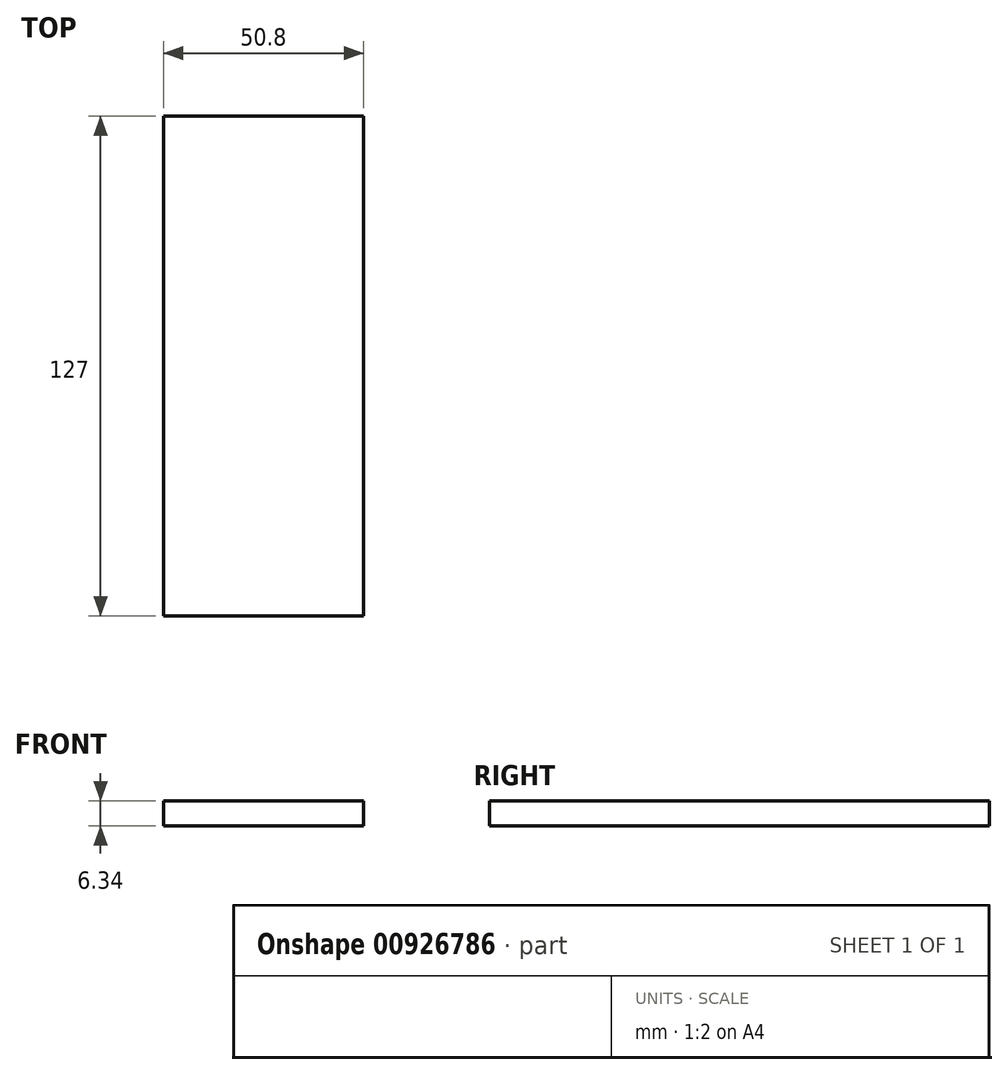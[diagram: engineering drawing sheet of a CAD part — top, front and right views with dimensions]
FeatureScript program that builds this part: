
annotation { "Feature Type Name" : "Feature", "Feature Type Description" : "" }
export const myFeature = defineFeature(function(context is Context, id is Id, definition is map)
    precondition{}
    {
        {
            var Q0;
            Q0=qCreatedBy(makeId("Front.planeOp"),FACE);
            var sketch = newSketch(context, id + "F0", { "sketchPlane" : qUnion([Q0])});
            skLineSegment(sketch, "E0.bottom", {"start": v(25.4, 3.18) * mm, "end": v(-25.4, 3.18) * mm});
            skLineSegment(sketch, "E0.top", {"start": v(25.4, -3.17) * mm, "end": v(-25.4, -3.17) * mm});
            skLineSegment(sketch, "E0.left", {"start": v(25.4, 3.18) * mm, "end": v(25.4, -3.17) * mm});
            skLineSegment(sketch, "E0.right", {"start": v(-25.4, 3.18) * mm, "end": v(-25.4, -3.17) * mm});
            skPoint(sketch, "E0.middle", {"position": v(0, 0) * mm});
            skSolve(sketch);
        }
        {
            var Q0;
            Q0=makeQuery(id+"F0.imprint","IMPRINT",FACE,{"disambiguationData":[TD([[makeQuery(id+"F0.imprint","IMPRINT",EDGE,{"derivedFrom":sQuery(id+"F0.wireOp",EDGE,"E0.bottom")}),1.0]])]});
            extrude(context, id + "F1", {"entities" : qUnion([Q0]), "depth" : 127 * mm, "offsetDistance" : 25.4 * mm});
        }
    });
